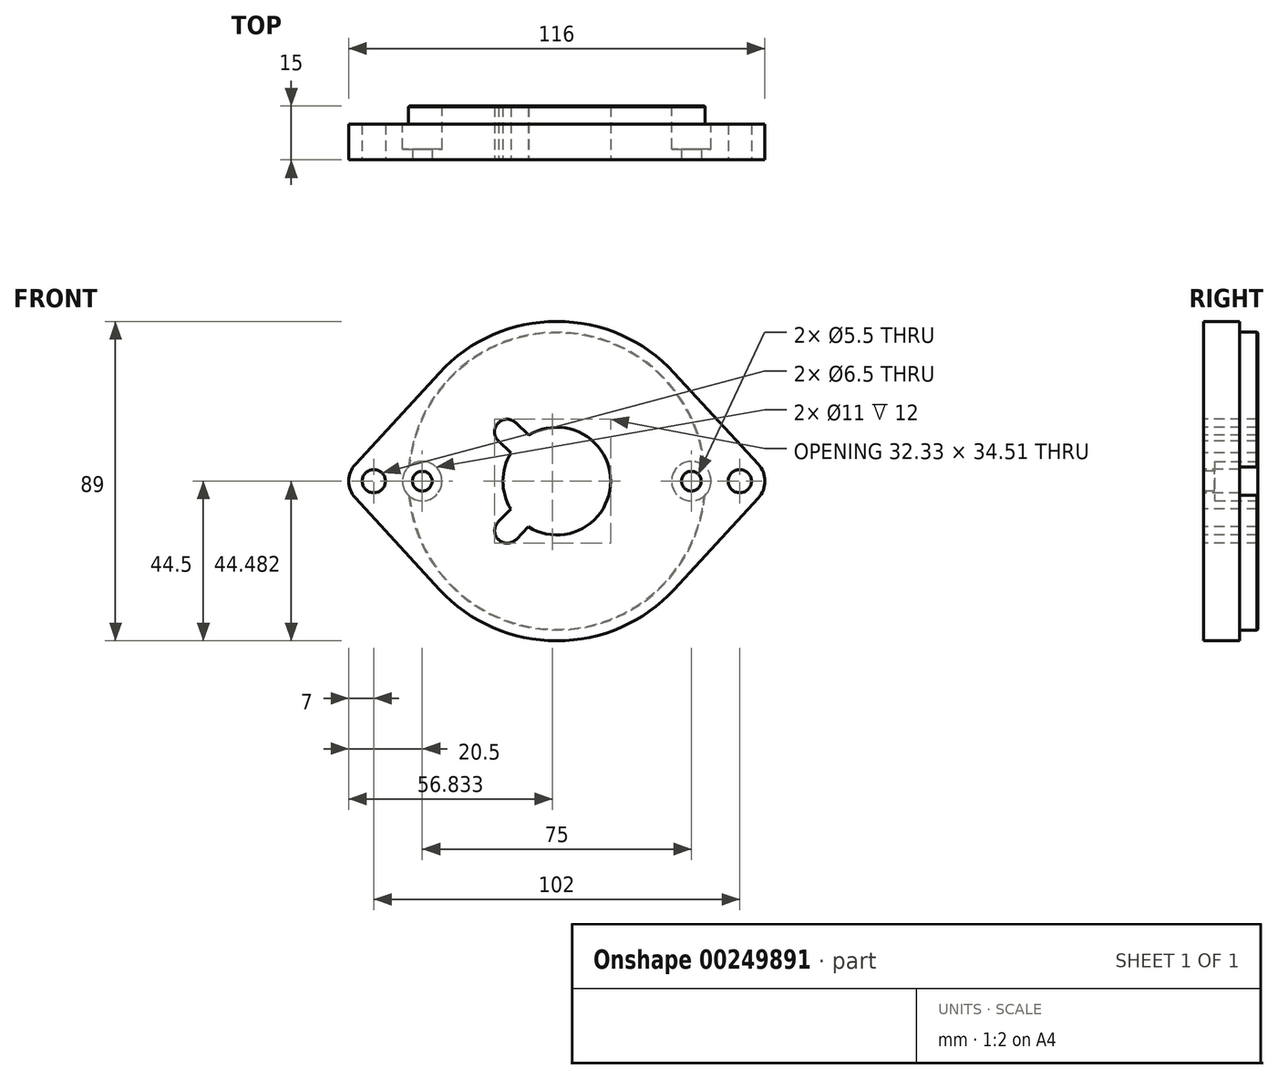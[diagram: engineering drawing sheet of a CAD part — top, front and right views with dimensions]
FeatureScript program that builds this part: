
annotation { "Feature Type Name" : "Feature", "Feature Type Description" : "" }
export const myFeature = defineFeature(function(context is Context, id is Id, definition is map)
    precondition{}
    {
        {
            var Q0;
            Q0=qCreatedBy(makeId("Front.planeOp"),FACE);
            var sketch = newSketch(context, id + "F0", { "sketchPlane" : qUnion([Q0])});
            skArc(sketch, "E0", {"start": v(-7.92, -12.74) * mm, "mid": v(14.94, -1.34) * mm, "end": v(-5.53, 13.94) * mm});
            skCircle(sketch, "E1", {"center": v(0, 0) * mm, "radius": 41.5 * mm});
            skArc(sketch, "E2", {"start": v(32.72, 30.16) * mm, "mid": v(0, 44.5) * mm, "end": v(-32.72, 30.16) * mm});
            skCircle(sketch, "E3", {"center": v(51, 0) * mm, "radius": 3.25 * mm});
            skCircle(sketch, "E4", {"center": v(-51, 0) * mm, "radius": 3.25 * mm});
            skPoint(sketch, "E5.visualSharp", {"position": v(-55.02, 0) * mm});
            skArc(sketch, "E6", {"start": v(56.15, -4.74) * mm, "mid": v(58, 0) * mm, "end": v(56.15, 4.74) * mm});
            skLineSegment(sketch, "E7", {"start": v(32.72, 30.16) * mm, "end": v(56.15, 4.74) * mm});
            skLineSegment(sketch, "E8", {"start": v(32.72, -30.16) * mm, "end": v(56.15, -4.74) * mm});
            skArc(sketch, "E9", {"start": v(-56.15, 4.74) * mm, "mid": v(-58, 0) * mm, "end": v(-56.15, -4.74) * mm});
            skLineSegment(sketch, "E10", {"start": v(-56.15, 4.74) * mm, "end": v(-32.72, 30.16) * mm});
            skLineSegment(sketch, "E11", {"start": v(-56.15, -4.74) * mm, "end": v(-32.72, -30.16) * mm});
            skArc(sketch, "E12.trimOffspring", {"start": v(-32.72, -30.16) * mm, "mid": v(0, -44.5) * mm, "end": v(32.72, -30.16) * mm});
            skCircle(sketch, "E13", {"center": v(-37.5, 0) * mm, "radius": 2.75 * mm});
            skCircle(sketch, "E14", {"center": v(37.5, 0) * mm, "radius": 2.75 * mm});
            skArc(sketch, "E15", {"start": v(-16.31, -11.33) * mm, "mid": v(-16.24, -16.28) * mm, "end": v(-11.3, -16.21) * mm});
            skLineSegment(sketch, "E16", {"start": v(-16.31, -11.33) * mm, "end": v(-12.84, -7.76) * mm});
            skLineSegment(sketch, "E17", {"start": v(-11.3, -16.21) * mm, "end": v(-7.92, -12.74) * mm});
            skArc(sketch, "E18.trimOffspring", {"start": v(-12.97, 7.54) * mm, "mid": v(-15, -0.13) * mm, "end": v(-12.84, -7.76) * mm});
            skLineSegment(sketch, "E19", {"start": v(-58, 0) * mm, "end": v(61.3, 0) * mm, "construction": true});
            skPoint(sketch, "E19.endSnap0", {"position": v(58, 0) * mm});
            skArc(sketch, "E20", {"start": v(-5.53, 13.94) * mm, "mid": v(-6.7, 13.42) * mm, "end": v(-7.84, 12.79) * mm});
            skLineSegment(sketch, "E21", {"start": v(-16.2, 11.15) * mm, "end": v(-12.79, 7.84) * mm});
            skLineSegment(sketch, "E22", {"start": v(-11.4, 16.25) * mm, "end": v(-7.84, 12.79) * mm});
            skArc(sketch, "E23.trimOffspring", {"start": v(-12.79, 7.84) * mm, "mid": v(-12.88, 7.7) * mm, "end": v(-12.97, 7.54) * mm});
            skArc(sketch, "E24", {"start": v(-11.4, 16.25) * mm, "mid": v(-16.39, 16.14) * mm, "end": v(-16.2, 11.15) * mm});
            skSolve(sketch);
        }
        {
            var Q0;
            Q0=makeQuery(id+"F0.imprint","IMPRINT",FACE,{"disambiguationData":[TD([[makeQuery(id+"F0.imprint","IMPRINT",EDGE,{"derivedFrom":sQuery(id+"F0.wireOp",EDGE,"E1")}),-1.0]])]});
            var Q1;
            Q1=makeQuery(id+"F0.imprint","IMPRINT",FACE,{"disambiguationData":[TD([[makeQuery(id+"F0.imprint","IMPRINT",EDGE,{"derivedFrom":sQuery(id+"F0.wireOp",EDGE,"E0")}),-1.0]])]});
            extrude(context, id + "F1", {"entities" : qUnion([Q0, Q1]), "oppositeDirection" : true, "depth" : 10 * mm});
        }
        {
            var Q0;
            Q0=makeQuery(id+"F0.imprint","IMPRINT",FACE,{"disambiguationData":[TD([[makeQuery(id+"F0.imprint","IMPRINT",EDGE,{"derivedFrom":sQuery(id+"F0.wireOp",EDGE,"E0")}),-1.0]])]});
            extrude(context, id + "F2", {"entities" : qUnion([Q0]), "operationType" : NewBodyOperationType.ADD, "oppositeDirection" : true, "depth" : 15 * mm});
        }
        {
            var Q0;
            Q0=makeQuery(id+"F2.opExtrude","CAP_FACE",FACE,{"disambiguationData":[OSD([sQuery(id+"F0.wireOp",EDGE,"E0"),sQuery(id+"F0.wireOp",EDGE,"E1"),sQuery(id+"F0.wireOp",EDGE,"E13"),sQuery(id+"F0.wireOp",EDGE,"E14")])],"isStart":false});
            var sketch = newSketch(context, id + "F3", { "sketchPlane" : qUnion([Q0])});
            skCircle(sketch, "E25", {"center": v(37.5, 0) * mm, "radius": 5.5 * mm});
            skCircle(sketch, "E26", {"center": v(-37.5, 0) * mm, "radius": 5.5 * mm});
            skSolve(sketch);
        }
        {
            var Q0;
            {var subQ0=sQuery(id+"F3.wireOp",EDGE,"E26");var subQ1=makeQuery(id+"F2.opExtrude","CAP_EDGE",EDGE,{"disambiguationData":[OSD([sQuery(id+"F0.wireOp",EDGE,"E1")])],"isStart":false});var subQ2=makeQuery(id+"F3.imprint","INTERSECT",VERTEX,{"disambiguationData":[OD(0.0)],"derivedFrom":[subQ1,subQ0]});Q0=makeQuery(id+"F3.imprint","IMPRINT",FACE,{"disambiguationData":[TD([[makeQuery(id+"F3.imprint","IMPRINT",EDGE,{"disambiguationData":[TD([[subQ2,1.0]])],"derivedFrom":subQ0}),1.0]])]});}
            var Q1;
            Q1=makeQuery(id+"F3.imprint","IMPRINT",FACE,{"disambiguationData":[TD([[makeQuery(id+"F3.imprint","IMPRINT",EDGE,{"derivedFrom":makeQuery(id+"F2.opExtrude","CAP_EDGE",EDGE,{"disambiguationData":[OSD([sQuery(id+"F0.wireOp",EDGE,"E14")])],"isStart":false})}),1.0]])]});
            var Q2;
            Q2=makeQuery(id+"F3.imprint","IMPRINT",FACE,{"disambiguationData":[TD([[makeQuery(id+"F3.imprint","IMPRINT",EDGE,{"derivedFrom":makeQuery(id+"F2.opExtrude","CAP_EDGE",EDGE,{"disambiguationData":[OSD([sQuery(id+"F0.wireOp",EDGE,"E13")])],"isStart":false})}),1.0]])]});
            var Q3;
            {var subQ0=sQuery(id+"F3.wireOp",EDGE,"E25");var subQ1=makeQuery(id+"F2.opExtrude","CAP_EDGE",EDGE,{"disambiguationData":[OSD([sQuery(id+"F0.wireOp",EDGE,"E1")])],"isStart":false});var subQ2=makeQuery(id+"F3.imprint","INTERSECT",VERTEX,{"disambiguationData":[OD(0.0)],"derivedFrom":[subQ1,subQ0]});Q3=makeQuery(id+"F3.imprint","IMPRINT",FACE,{"disambiguationData":[TD([[makeQuery(id+"F3.imprint","IMPRINT",EDGE,{"disambiguationData":[TD([[subQ2,-1.0]])],"derivedFrom":subQ0}),1.0]])]});}
            extrude(context, id + "F4", {"entities" : qUnion([Q0, Q1, Q2, Q3]), "operationType" : NewBodyOperationType.REMOVE, "oppositeDirection" : true, "depth" : 12 * mm});
        }
        {
            var Q0;
            Q0=makeQuery(id+"F4.boolean.opBoolean","SPLIT",EDGE,{"disambiguationData":[OD(1.0)],"derivedFrom":makeQuery(id+"F2.opExtrude","CAP_EDGE",EDGE,{"disambiguationData":[OSD([sQuery(id+"F0.wireOp",EDGE,"E1")])],"isStart":false})});
            var Q1;
            Q1=makeQuery(id+"F4.boolean.opBoolean","SPLIT",EDGE,{"disambiguationData":[OD(0.0)],"derivedFrom":makeQuery(id+"F2.opExtrude","CAP_EDGE",EDGE,{"disambiguationData":[OSD([sQuery(id+"F0.wireOp",EDGE,"E1")])],"isStart":false})});
            chamfer(context, id + "F5", {"entities" : qUnion([Q0, Q1]), "width" : 0.2 * mm, "tangentPropagation" : true});
        }
    });
